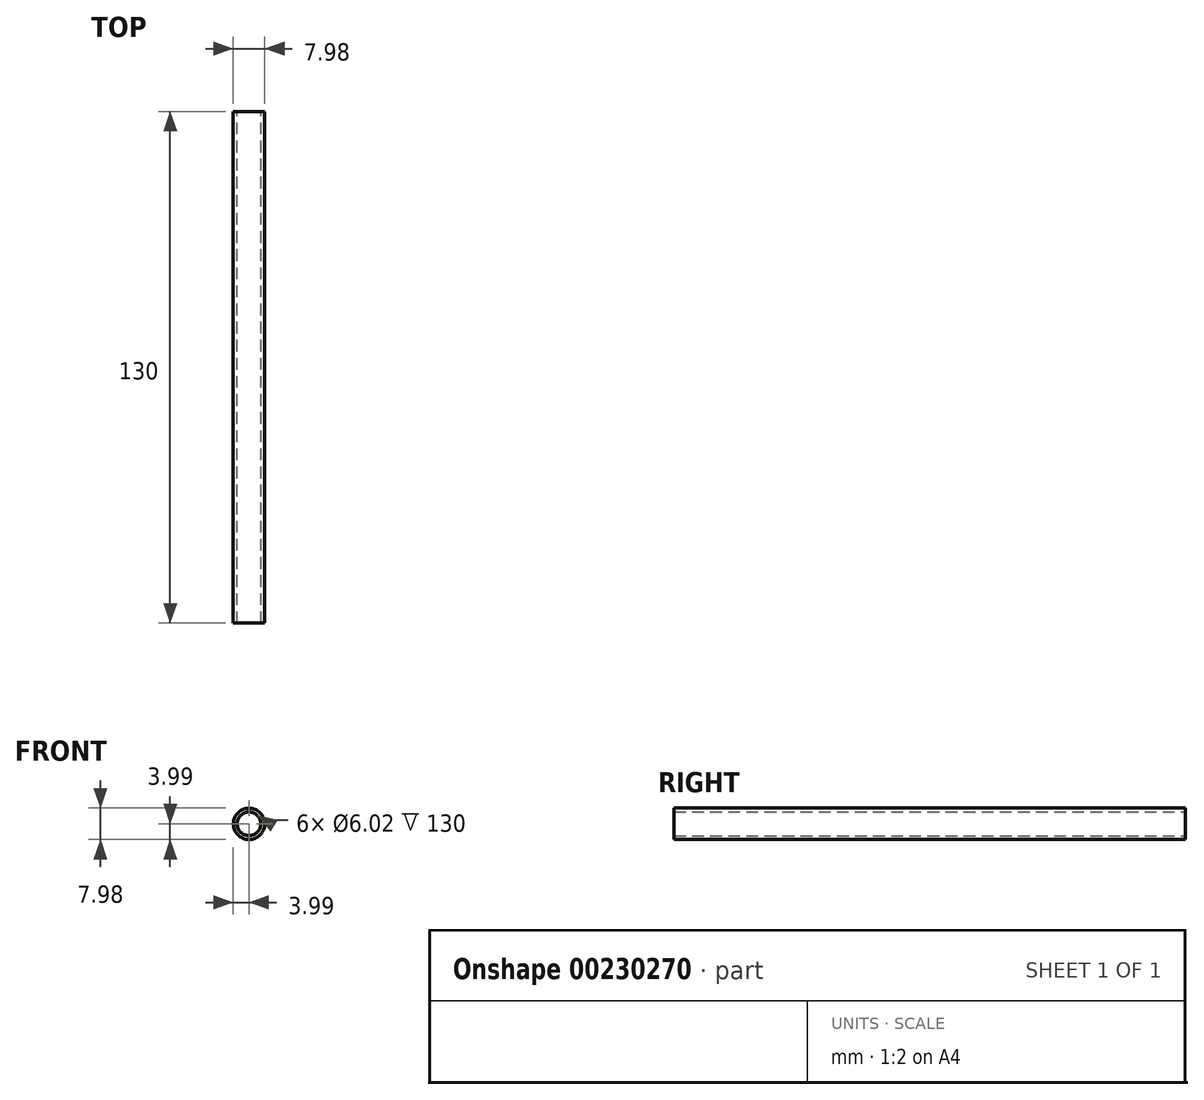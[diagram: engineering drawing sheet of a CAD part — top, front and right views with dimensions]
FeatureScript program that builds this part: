
annotation { "Feature Type Name" : "Feature", "Feature Type Description" : "" }
export const myFeature = defineFeature(function(context is Context, id is Id, definition is map)
    precondition{}
    {
        {
            var Q0;
            Q0=qCreatedBy(makeId("Front.planeOp"),FACE);
            var sketch = newSketch(context, id + "F0", { "sketchPlane" : qUnion([Q0])});
            skCircle(sketch, "E0", {"center": v(0, 0) * mm, "radius": 4 * mm});
            skCircle(sketch, "E1", {"center": v(0, 0) * mm, "radius": 3 * mm});
            skSolve(sketch);
        }
        {
            var Q0;
            Q0=makeQuery(id+"F0.imprint","IMPRINT",FACE,{"disambiguationData":[TD([[makeQuery(id+"F0.imprint","IMPRINT",EDGE,{"derivedFrom":sQuery(id+"F0.wireOp",EDGE,"E0")}),1.0]])]});
            extrude(context, id + "F1", {"entities" : qUnion([Q0]), "endBound" : BoundingType.SYMMETRIC, "depth" : 130 * mm});
        }
    });
